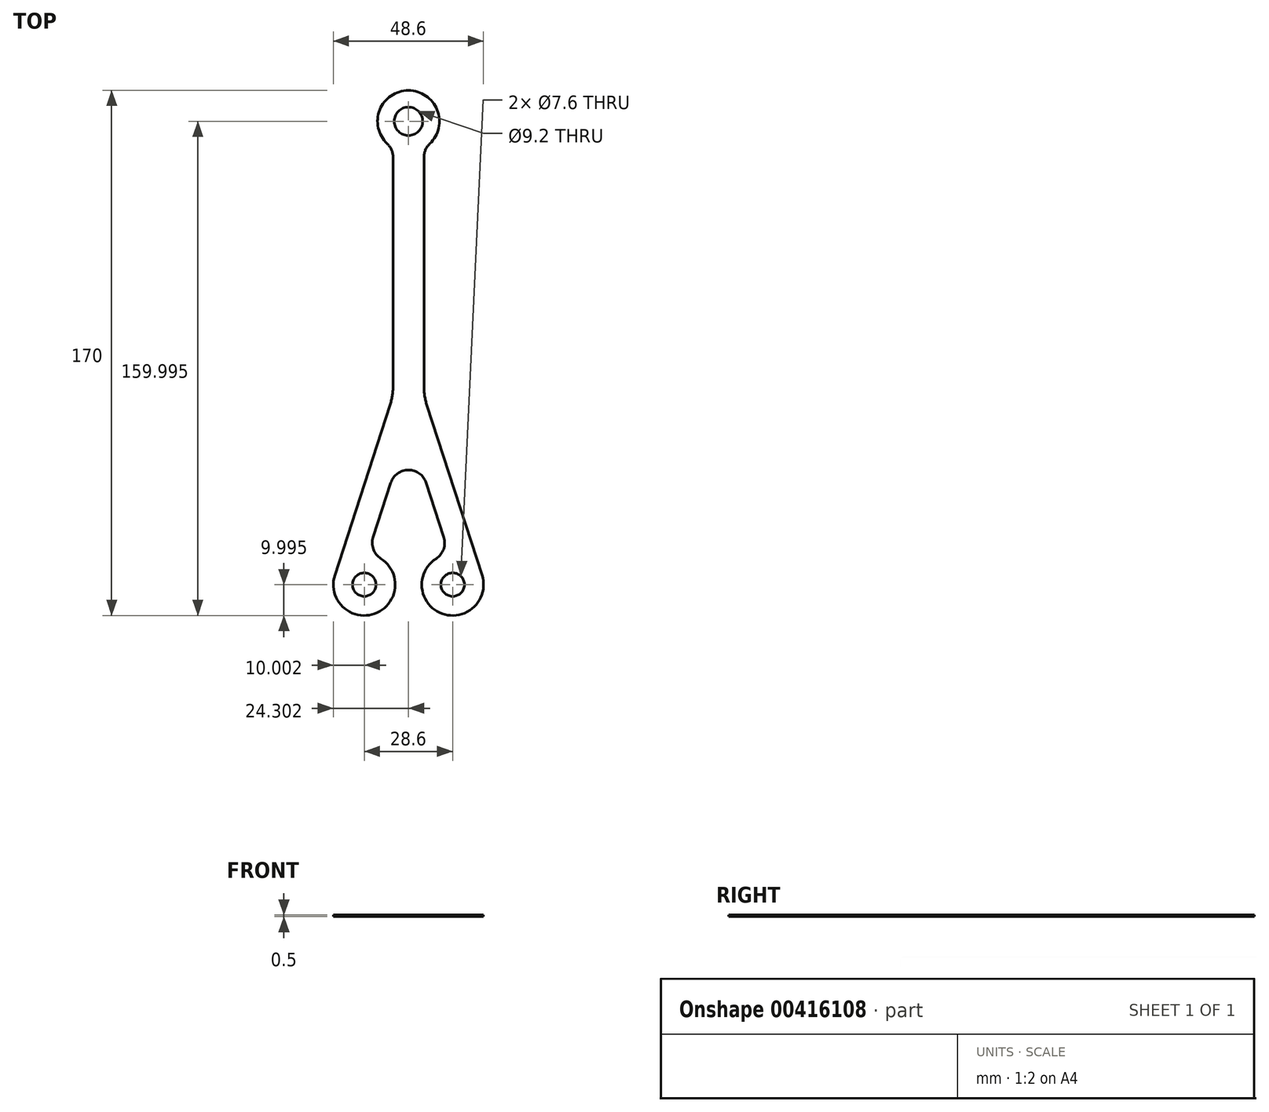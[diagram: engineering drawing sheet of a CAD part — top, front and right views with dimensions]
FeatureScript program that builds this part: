
annotation { "Feature Type Name" : "Feature", "Feature Type Description" : "" }
export const myFeature = defineFeature(function(context is Context, id is Id, definition is map)
    precondition{}
    {
        {
            var Q0;
            Q0=qCreatedBy(makeId("Top.planeOp"),FACE);
            var sketch = newSketch(context, id + "F0", { "sketchPlane" : qUnion([Q0])});
            skArc(sketch, "E0", {"start": v(26.24, 43.65) * mm, "mid": v(19.36, 60.92) * mm, "end": v(12.49, 43.65) * mm});
            skCircle(sketch, "E1", {"center": v(19.36, 50.92) * mm, "radius": 4.6 * mm});
            skArc(sketch, "E2", {"start": v(-4.45, -96) * mm, "mid": v(8.45, -108.5) * mm, "end": v(10.43, -90.65) * mm});
            skCircle(sketch, "E3", {"center": v(5.06, -99.08) * mm, "radius": 3.8 * mm});
            skArc(sketch, "E4", {"start": v(28.3, -90.65) * mm, "mid": v(30.28, -108.5) * mm, "end": v(43.17, -96) * mm});
            skCircle(sketch, "E5", {"center": v(33.66, -99.08) * mm, "radius": 3.8 * mm});
            skLineSegment(sketch, "E6.left", {"start": v(14.36, -34.85) * mm, "end": v(14.36, 39.3) * mm});
            skLineSegment(sketch, "E6.right", {"start": v(24.36, -34.85) * mm, "end": v(24.36, 39.3) * mm});
            skLineSegment(sketch, "E7", {"start": v(19.36, 50.92) * mm, "end": v(19.36, 50.92) * mm});
            skLineSegment(sketch, "E8", {"start": v(-4.45, -96) * mm, "end": v(13.39, -41.03) * mm});
            skLineSegment(sketch, "E9", {"start": v(19.36, 50.92) * mm, "end": v(19.36, -109.69) * mm, "construction": true});
            skLineSegment(sketch, "E10.MirrorCS", {"start": v(30.78, -83.73) * mm, "end": v(25.07, -66.12) * mm});
            skLineSegment(sketch, "E11.MirrorCS", {"start": v(43.17, -96) * mm, "end": v(25.34, -41.03) * mm});
            skLineSegment(sketch, "E12.trimOffspring", {"start": v(7.94, -83.73) * mm, "end": v(13.66, -66.12) * mm});
            skPoint(sketch, "E13.visualSharp", {"position": v(6.18, -89.15) * mm});
            skArc(sketch, "E13.filletArc", {"start": v(7.94, -83.73) * mm, "mid": v(8, -87.61) * mm, "end": v(10.43, -90.65) * mm});
            skPoint(sketch, "E14.visualSharp", {"position": v(32.54, -89.15) * mm});
            skArc(sketch, "E14.filletArc", {"start": v(28.3, -90.65) * mm, "mid": v(30.72, -87.61) * mm, "end": v(30.78, -83.73) * mm});
            skPoint(sketch, "E15.visualSharp", {"position": v(19.36, -48.53) * mm});
            skArc(sketch, "E15.filletArc", {"start": v(25.07, -66.12) * mm, "mid": v(19.36, -61.97) * mm, "end": v(13.66, -66.12) * mm});
            skPoint(sketch, "E16.visualSharp", {"position": v(14.36, -38.02) * mm});
            skArc(sketch, "E16.filletArc", {"start": v(13.39, -41.03) * mm, "mid": v(14.12, -37.98) * mm, "end": v(14.36, -34.85) * mm});
            skPoint(sketch, "E17.visualSharp", {"position": v(24.36, -38.02) * mm});
            skArc(sketch, "E17.filletArc", {"start": v(24.36, -34.85) * mm, "mid": v(24.6, -37.98) * mm, "end": v(25.34, -41.03) * mm});
            skPoint(sketch, "E18.visualSharp", {"position": v(24.36, 42.26) * mm});
            skArc(sketch, "E18.filletArc", {"start": v(26.24, 43.65) * mm, "mid": v(24.85, 41.67) * mm, "end": v(24.36, 39.3) * mm});
            skPoint(sketch, "E19.visualSharp", {"position": v(14.36, 42.26) * mm});
            skArc(sketch, "E19.filletArc", {"start": v(14.36, 39.3) * mm, "mid": v(13.87, 41.67) * mm, "end": v(12.49, 43.65) * mm});
            skSolve(sketch);
        }
        {
            var Q0;
            {var subQ3=sQuery(id+"F0.wireOp",EDGE,"E11.MirrorCS");Q0=makeQuery(id+"F0.imprint","IMPRINT",FACE,{"disambiguationData":[TD([[makeQuery(id+"F0.imprint","IMPRINT",EDGE,{"derivedFrom":subQ3}),1.0]])]});}
            var Q1;
            {var subQ0=sQuery(id+"F0.wireOp",EDGE,"17e8885f-d974-4633-8da8-e6ac48455fc4.0");var subQ1=sQuery(id+"F0.wireOp",EDGE,"E6.bottom");var subQ2=makeQuery(id+"F0.imprint","INTERSECT",VERTEX,{"derivedFrom":[subQ1,subQ0]});Q1=makeQuery(id+"F0.imprint","IMPRINT",FACE,{"disambiguationData":[TD([[makeQuery(id+"F0.imprint","IMPRINT",EDGE,{"disambiguationData":[TD([[subQ2,-1.0]])],"derivedFrom":subQ1}),1.0]])]});}
            var Q2;
            {var subQ0=sQuery(id+"F0.wireOp",EDGE,"E6.left");var subQ11=sQuery(id+"F0.wireOp",EDGE,"E0");var subQ12=makeQuery(id+"F0.imprint","INTERSECT",VERTEX,{"derivedFrom":[subQ11,subQ0]});Q2=makeQuery(id+"F0.imprint","IMPRINT",FACE,{"disambiguationData":[TD([[makeQuery(id+"F0.imprint","IMPRINT",EDGE,{"disambiguationData":[TD([[subQ12,-1.0]])],"derivedFrom":subQ11}),-1.0]])]});}
            var Q3;
            {var subQ3=sQuery(id+"F0.wireOp",EDGE,"c1efcac0-5ad7-496a-8be3-88102d86ed780.MirrorCS");Q3=makeQuery(id+"F0.imprint","IMPRINT",FACE,{"disambiguationData":[TD([[makeQuery(id+"F0.imprint","IMPRINT",EDGE,{"derivedFrom":subQ3}),-1.0]])]});}
            var Q4;
            Q4=makeQuery(id+"F0.imprint","IMPRINT",FACE,{"disambiguationData":[TD([[makeQuery(id+"F0.imprint","IMPRINT",EDGE,{"derivedFrom":sQuery(id+"F0.wireOp",EDGE,"E5")}),-1.0]])]});
            var Q5;
            Q5=makeQuery(id+"F0.imprint","IMPRINT",FACE,{"disambiguationData":[TD([[makeQuery(id+"F0.imprint","IMPRINT",EDGE,{"derivedFrom":sQuery(id+"F0.wireOp",EDGE,"E3")}),-1.0]])]});
            var Q6;
            {var subQ0=sQuery(id+"F0.wireOp",EDGE,"zfR5ejOt-fnXG-8KqO-cYpp-28Waz7bZxska.bottom");var subQ1=sQuery(id+"F0.wireOp",EDGE,"E0");var subQ5=makeQuery(id+"F0.imprint","INTERSECT",VERTEX,{"disambiguationData":[OD(0.0)],"derivedFrom":[subQ1,subQ0]});Q6=makeQuery(id+"F0.imprint","IMPRINT",FACE,{"disambiguationData":[TD([[makeQuery(id+"F0.imprint","IMPRINT",EDGE,{"disambiguationData":[TD([[subQ5,1.0]])],"derivedFrom":subQ1}),1.0]])]});}
            var Q7;
            {var subQ0=sQuery(id+"F0.wireOp",EDGE,"zfR5ejOt-fnXG-8KqO-cYpp-28Waz7bZxska.bottom");var subQ1=sQuery(id+"F0.wireOp",EDGE,"E0");var subQ2=makeQuery(id+"F0.imprint","INTERSECT",VERTEX,{"disambiguationData":[OD(0.0)],"derivedFrom":[subQ1,subQ0]});Q7=makeQuery(id+"F0.imprint","IMPRINT",FACE,{"disambiguationData":[TD([[makeQuery(id+"F0.imprint","IMPRINT",EDGE,{"disambiguationData":[TD([[subQ2,-1.0]])],"derivedFrom":subQ1}),1.0]])]});}
            var Q8;
            {var subQ7=sQuery(id+"F0.wireOp",EDGE,"E6.left");var subQ9=sQuery(id+"F0.wireOp",EDGE,"E0");var subQ10=makeQuery(id+"F0.imprint","INTERSECT",VERTEX,{"derivedFrom":[subQ9,subQ7]});Q8=makeQuery(id+"F0.imprint","IMPRINT",FACE,{"disambiguationData":[TD([[makeQuery(id+"F0.imprint","IMPRINT",EDGE,{"disambiguationData":[TD([[subQ10,-1.0]])],"derivedFrom":subQ9}),1.0]])]});}
            var Q9;
            {var subQ0=sQuery(id+"F0.wireOp",EDGE,"zfR5ejOt-fnXG-8KqO-cYpp-28Waz7bZxska.bottom");var subQ1=sQuery(id+"F0.wireOp",EDGE,"E0");var subQ2=makeQuery(id+"F0.imprint","INTERSECT",VERTEX,{"disambiguationData":[OD(1.0)],"derivedFrom":[subQ1,subQ0]});Q9=makeQuery(id+"F0.imprint","IMPRINT",FACE,{"disambiguationData":[TD([[makeQuery(id+"F0.imprint","IMPRINT",EDGE,{"disambiguationData":[TD([[subQ2,1.0]])],"derivedFrom":subQ1}),1.0]])]});}
            extrude(context, id + "F1", {"entities" : qUnion([Q0, Q1, Q2, Q3, Q4, Q5, Q6, Q7, Q8, Q9]), "depth" : .5 * mm});
        }
    });
